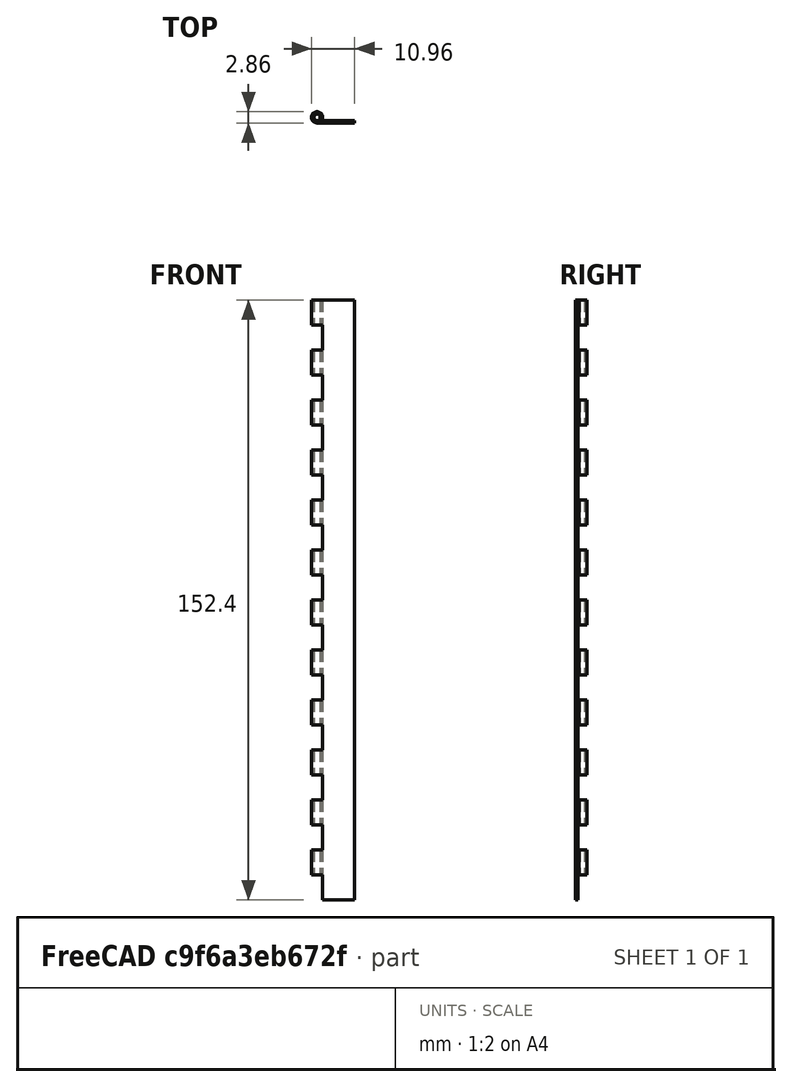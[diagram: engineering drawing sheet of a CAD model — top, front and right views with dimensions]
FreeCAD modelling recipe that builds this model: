
FCSTD DOCUMENT  (FreeCAD 0.19R24267 (Git))
Label: hinge_r-6
License: All rights reserved
LicenseURL: http://en.wikipedia.org/wiki/All_rights_reserved
objects: Part::Feature×1, Sketcher::SketchObject×1, Part::Extrusion×1, Part::Cut×1
note: 4 computed .brp shape members not serialized (recipe doc carries the construction recipe); baked Part::Feature solids carry a one-line shape summary decoded from their .brp

FEATURE [Part::Feature] Solid
  shape: bbox 10.95 x 2.858 x 304.8 mm, 244 faces (baked)
FEATURE [Sketcher::SketchObject] Sketch
  FullyConstrained = false
  MapMode = 5
  Placement = pos=(0,0,152.4) rot=(0,0,1;0rad)
  Support = -> [Solid]
  sketch-geometry (4):
    g0: LineSegment StartX=-3.61622 StartY=2.20045 StartZ=0 EndX=12.2431 EndY=2.20045 EndZ=0
    g1: LineSegment StartX=12.2431 StartY=2.20045 StartZ=0 EndX=12.2431 EndY=-2.92226 EndZ=0
    g2: LineSegment StartX=12.2431 StartY=-2.92226 StartZ=0 EndX=-3.61622 EndY=-2.92226 EndZ=0
    g3: LineSegment StartX=-3.61622 StartY=-2.92226 StartZ=0 EndX=-3.61622 EndY=2.20045 EndZ=0
  constraints (8):
    c: Coincident(g0,g1)
    c: Coincident(g1,g2)
    c: Coincident(g2,g3)
    c: Coincident(g3,g0)
    c: Horizontal(g0)
    c: Horizontal(g2)
    c: Vertical(g1)
    c: Vertical(g3)
FEATURE [Part::Extrusion] Extrude
  Base = -> Sketch
  Dir = (0,0,1)
  DirMode = 2
  FaceMakerClass = Part::FaceMakerBullseye
  LengthFwd = 0
  LengthRev = 152.4
  Solid = true
  Symmetric = false
FEATURE [Part::Cut] Cut
  Base = -> Solid
  Tool = -> Extrude
